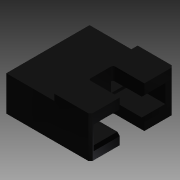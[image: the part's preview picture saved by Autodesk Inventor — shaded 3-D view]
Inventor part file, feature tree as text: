
AUTODESK INVENTOR PART (.ipt)
format: ipt  version: 2013 (Build 170138000, 138)  size: 172,544 bytes
history: native  units: in
note: dims shown in document units (in); Inventor stores cm internally (conversion verified against a paired STEP export)
features: extrude x4, sketch x4, chamfer x3, fillet x1, plane x1, mirror x1
ambient origin geometry x8: Origin, YZ Plane, XZ Plane, XY Plane, X Axis, Y Axis, Z Axis, Center Point
bodies: Solid1 (feature_tree)
feature tree (14):
  extrude  "Extrusion1"  Depth=0.098in
  extrude  "Extrusion2"  Depth=0.0857in
  chamfer  "Chamfer1"  Distance=0.198in
  extrude  "Extrusion3"  Depth=0.0582in
  extrude  "Extrusion4"  Depth=0.049in
  fillet  "Fillet1"  Radius=0.0582in
  chamfer  "Chamfer2"  Distance=0.0171in
  plane  "Work Plane1"
  mirror  "Mirror1"
  chamfer  "Chamfer3"  Distance=0.0291in
  sketch  "Sketch1"  dims[d0=0.2in d1=0.098in]
  sketch  "Sketch2"  dims[d2=0.083in d3=0.0857in d4=0.198in d5=0.0in]
  sketch  "Sketch3"  dims[d6=0.0582in d7=0.0582in]
  sketch  "Sketch4"  dims[d8=0.049in d9=0.049in d10=0.0582in d11=0.0171in d12=0.0291in d13=0.0291in d14=0.198in d15=0.0in d16=0.015in d17=0.125in d18=45.0deg d22=0.198in d23=0.0in d24=0.0582in d25=0.0743in d26=0.198in d27=0.0in d28=0.005in d29=0.005in d30=0.125in d31=45.0deg d32=0.17in d33=0.043in d34=0.006in d35=0.125in d36=45.0deg]
